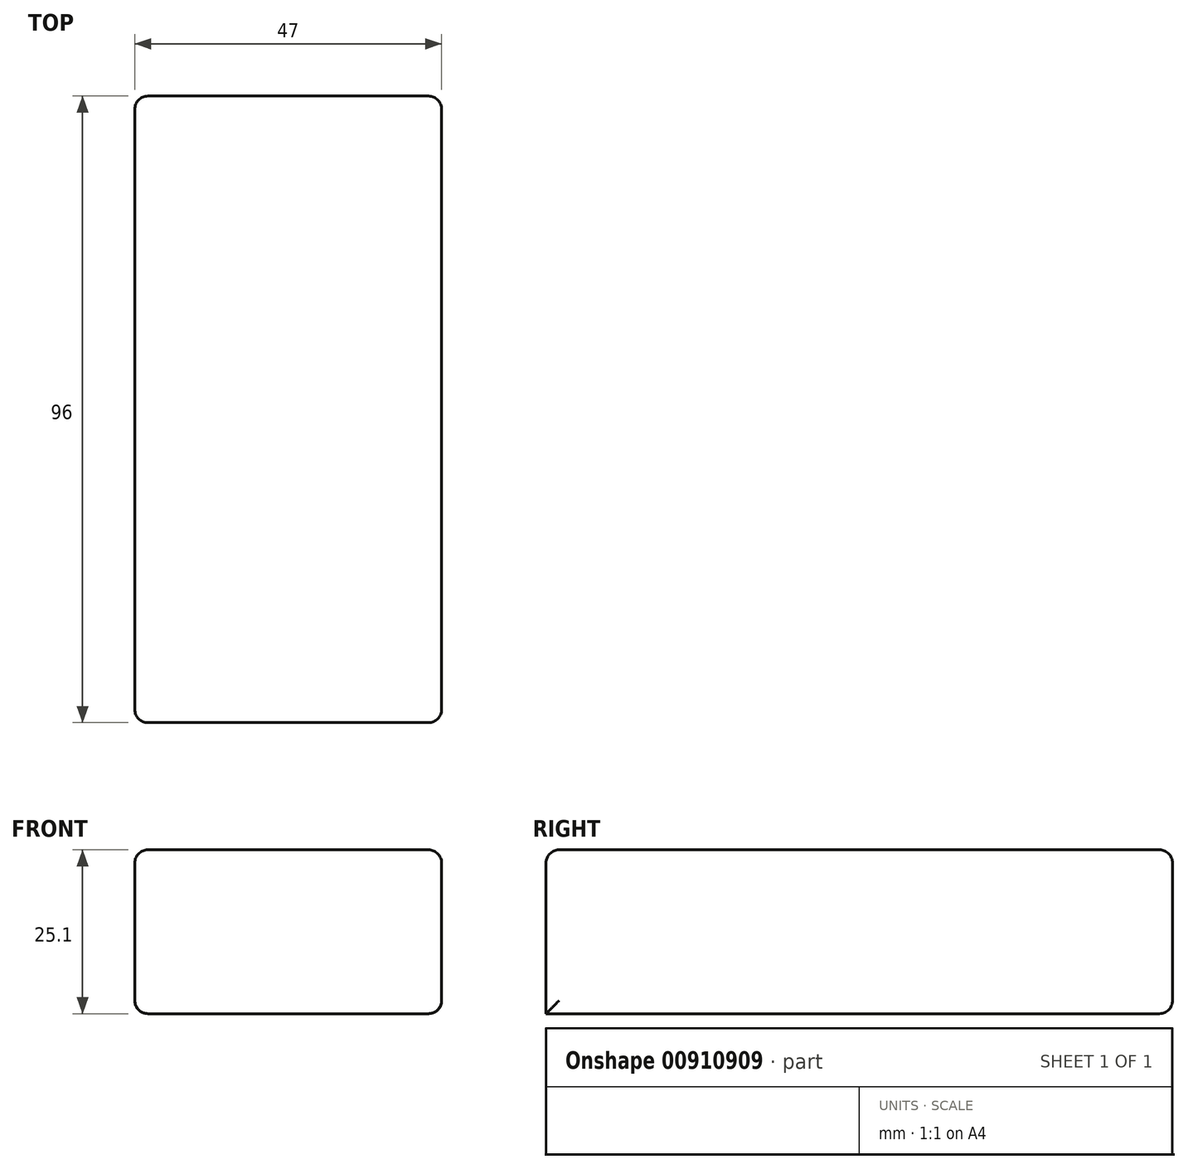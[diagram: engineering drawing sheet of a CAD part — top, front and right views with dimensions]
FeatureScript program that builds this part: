
annotation { "Feature Type Name" : "Feature", "Feature Type Description" : "" }
export const myFeature = defineFeature(function(context is Context, id is Id, definition is map)
    precondition{}
    {
        {
            var Q0;
            Q0=qCreatedBy(makeId("Top.planeOp"),FACE);
            var sketch = newSketch(context, id + "F0", { "sketchPlane" : qUnion([Q0])});
            skLineSegment(sketch, "E0.bottom", {"start": v(-586.76, 1219.2) * mm, "end": v(586.76, 1219.2) * mm});
            skLineSegment(sketch, "E0.top", {"start": v(-586.76, -1219.2) * mm, "end": v(586.76, -1219.2) * mm});
            skLineSegment(sketch, "E0.left", {"start": v(-586.76, 1219.2) * mm, "end": v(-586.76, -1219.2) * mm});
            skLineSegment(sketch, "E0.right", {"start": v(586.76, 1219.2) * mm, "end": v(586.76, -1219.2) * mm});
            skPoint(sketch, "E0.middle", {"position": v(0, 0) * mm});
            skLineSegment(sketch, "E1.bottom", {"start": v(-23.5, 48) * mm, "end": v(23.5, 48) * mm});
            skLineSegment(sketch, "E1.top", {"start": v(-23.5, -48) * mm, "end": v(23.5, -48) * mm});
            skLineSegment(sketch, "E1.left", {"start": v(-23.5, 48) * mm, "end": v(-23.5, -48) * mm});
            skLineSegment(sketch, "E1.right", {"start": v(23.5, 48) * mm, "end": v(23.5, -48) * mm});
            skSolve(sketch);
        }
        {
            var Q0;
            Q0=makeQuery(id+"F0.imprint","IMPRINT",FACE,{"disambiguationData":[TD([[makeQuery(id+"F0.imprint","IMPRINT",EDGE,{"derivedFrom":sQuery(id+"F0.wireOp",EDGE,"E1.bottom")}),-1.0]])]});
            extrude(context, id + "F1", {"entities" : qUnion([Q0]), "depth" : 25.1 * mm, "offsetDistance" : 25 * mm});
        }
        {
            var Q0;
            Q0=makeQuery(id+"F1.opExtrude","SWEPT_EDGE",EDGE,{"disambiguationData":[OSD([sQuery(id+"F0.wireOp",EDGE,"E1.top"),sQuery(id+"F0.wireOp",EDGE,"E1.left")])]});
            var Q1;
            Q1=makeQuery(id+"F1.opExtrude","CAP_EDGE",EDGE,{"disambiguationData":[OSD([sQuery(id+"F0.wireOp",EDGE,"E1.top")])],"isStart":false});
            var Q2;
            Q2=makeQuery(id+"F1.opExtrude","CAP_EDGE",EDGE,{"disambiguationData":[OSD([sQuery(id+"F0.wireOp",EDGE,"E1.left")])],"isStart":false});
            var Q3;
            Q3=makeQuery(id+"F1.opExtrude","CAP_EDGE",EDGE,{"disambiguationData":[OSD([sQuery(id+"F0.wireOp",EDGE,"E1.right")])],"isStart":false});
            var Q4;
            Q4=makeQuery(id+"F1.opExtrude","SWEPT_EDGE",EDGE,{"disambiguationData":[OSD([sQuery(id+"F0.wireOp",EDGE,"E1.top"),sQuery(id+"F0.wireOp",EDGE,"E1.right")])]});
            var Q5;
            Q5=makeQuery(id+"F1.opExtrude","CAP_EDGE",EDGE,{"disambiguationData":[OSD([sQuery(id+"F0.wireOp",EDGE,"E1.right")])],"isStart":true});
            var Q6;
            Q6=makeQuery(id+"F1.opExtrude","SWEPT_EDGE",EDGE,{"disambiguationData":[OSD([sQuery(id+"F0.wireOp",EDGE,"E1.bottom"),sQuery(id+"F0.wireOp",EDGE,"E1.right")])]});
            var Q7;
            Q7=makeQuery(id+"F1.opExtrude","CAP_EDGE",EDGE,{"disambiguationData":[OSD([sQuery(id+"F0.wireOp",EDGE,"E1.bottom")])],"isStart":false});
            var Q8;
            Q8=makeQuery(id+"F1.opExtrude","SWEPT_EDGE",EDGE,{"disambiguationData":[OSD([sQuery(id+"F0.wireOp",EDGE,"E1.bottom"),sQuery(id+"F0.wireOp",EDGE,"E1.left")])]});
            var Q9;
            Q9=makeQuery(id+"F1.opExtrude","CAP_EDGE",EDGE,{"disambiguationData":[OSD([sQuery(id+"F0.wireOp",EDGE,"E1.left")])],"isStart":true});
            var Q10;
            Q10=makeQuery(id+"F1.opExtrude","CAP_EDGE",EDGE,{"disambiguationData":[OSD([sQuery(id+"F0.wireOp",EDGE,"E1.bottom")])],"isStart":true});
            fillet(context, id + "F2", {"entities" : qUnion([Q0, Q1, Q2, Q3, Q4, Q5, Q6, Q7, Q8, Q9, Q10]), "radius" : 2 * mm, "tangentPropagation" : true, "allowEdgeOverflow" : false});
        }
    });
